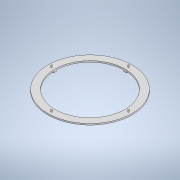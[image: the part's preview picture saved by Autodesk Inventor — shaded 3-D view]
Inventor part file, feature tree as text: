
AUTODESK INVENTOR PART (.ipt)
format: ipt  version: 2021 (Build 250183000, 183)  size: 162,816 bytes
history: native  units: mm
features: extrude x3, sketch x3, other x1
ambient origin geometry x8: Origin, YZ Plane, XZ Plane, XY Plane, X Axis, Y Axis, Z Axis, Center Point
bodies: Body1 (feature_tree)
feature tree (7):
  other  "Sólido1"
  extrude  "Extrusión1"  Depth=100.0mm
  extrude  "Extrusión2"  Depth=2.0mm TaperAngle=0.0deg
  extrude  "Extrusión3"  Depth=2.0mm TaperAngle=360.0deg
  sketch  "Boceto1"  dims[d0=120.0mm d1=100.0mm]
  sketch  "Boceto2"  dims[d2=2.3mm d3=2.0mm d4=0.0mm]
  sketch  "Boceto3"  dims[d5=2.3mm d6=40.0mm d8=360.0deg d10=2.0mm d11=0.0mm d13=3.0mm d14=100.0mm d15=60.0mm d17=360.0deg d19=40.0mm d21=360.0deg d23=2.0mm d24=0.0mm]
